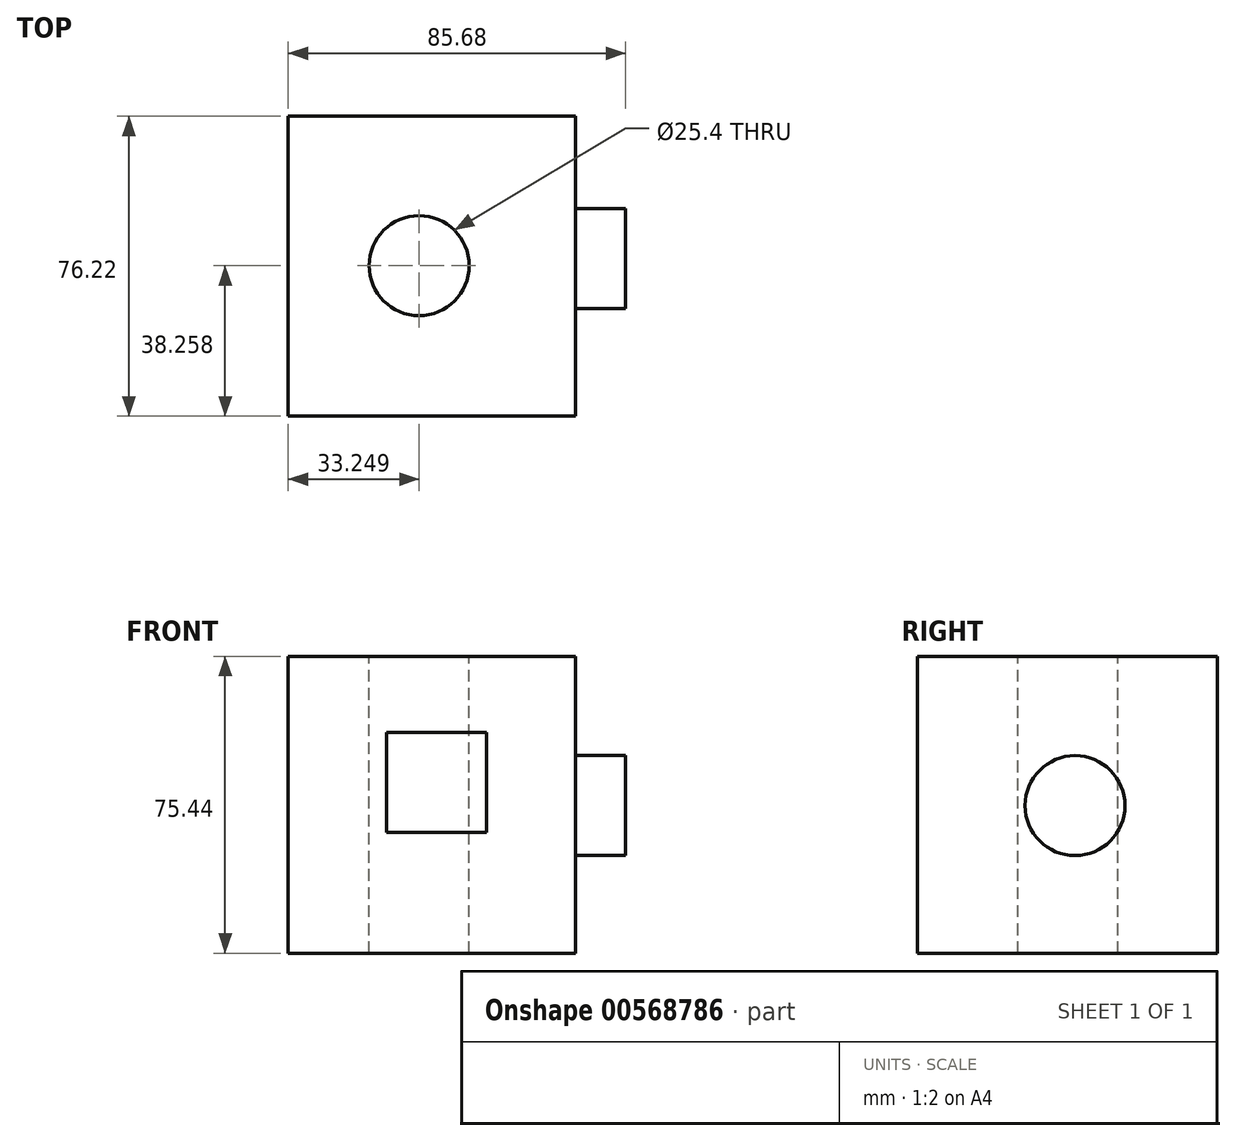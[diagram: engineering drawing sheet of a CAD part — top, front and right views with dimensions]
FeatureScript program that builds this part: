
annotation { "Feature Type Name" : "Feature", "Feature Type Description" : "" }
export const myFeature = defineFeature(function(context is Context, id is Id, definition is map)
    precondition{}
    {
        {
            var Q0;
            Q0=qCreatedBy(makeId("Front.planeOp"),FACE);
            var sketch = newSketch(context, id + "F0", { "sketchPlane" : qUnion([Q0])});
            skLineSegment(sketch, "E0.bottom", {"start": v(3.3, 0) * mm, "end": v(76.28, 0) * mm});
            skLineSegment(sketch, "E0.top", {"start": v(3.3, 75.44) * mm, "end": v(76.28, 75.44) * mm});
            skLineSegment(sketch, "E0.left", {"start": v(3.3, 0) * mm, "end": v(3.3, 75.44) * mm});
            skLineSegment(sketch, "E0.right", {"start": v(76.28, 0) * mm, "end": v(76.28, 75.44) * mm});
            skSolve(sketch);
        }
        {
            var Q0;
            Q0=makeQuery(id+"F0.imprint","IMPRINT",FACE,{"disambiguationData":[TD([[makeQuery(id+"F0.imprint","IMPRINT",EDGE,{"derivedFrom":sQuery(id+"F0.wireOp",EDGE,"E0.bottom")}),1.0]])]});
            extrude(context, id + "F1", {"entities" : qUnion([Q0]), "depth" : 76.2 * mm, "offsetDistance" : 25.4 * mm});
        }
        {
            var Q0;
            Q0=makeQuery(id+"F1.opExtrude","SWEPT_FACE",FACE,{"disambiguationData":[OSD([sQuery(id+"F0.wireOp",EDGE,"E0.top")])]});
            var sketch = newSketch(context, id + "F2", { "sketchPlane" : qUnion([Q0])});
            skPoint(sketch, "E1", {"position": v(36.55, -37.96) * mm});
            skSolve(sketch);
        }
        {
            var Q0;
            Q0=sQuery(id+"F2.wireOp",VERTEX,"E1");
            var Q1;
            Q1=makeQuery(id+"F1.opExtrude","SWEPT_BODY",BODY,{"disambiguationData":[OSD([sQuery(id+"F0.wireOp",EDGE,"E0.bottom"),sQuery(id+"F0.wireOp",EDGE,"E0.top"),sQuery(id+"F0.wireOp",EDGE,"E0.left"),sQuery(id+"F0.wireOp",EDGE,"E0.right")])]});
            hole(context, id + "F3", {"style" : HoleStyle.SIMPLE, "endStyle" : HoleEndStyle.THROUGH, "holeDiameter" : 25.4 * mm, "isTappedThrough" : true, "tappedDepth" : 12.7 * mm, "tapClearance" : 3, "locations" : qUnion([Q0]), "scope" : qUnion([Q1])});
        }
        {
            var Q0;
            Q0=makeQuery(id+"F1.opExtrude","CAP_FACE",FACE,{"disambiguationData":[OSD([sQuery(id+"F0.wireOp",EDGE,"E0.bottom"),sQuery(id+"F0.wireOp",EDGE,"E0.top"),sQuery(id+"F0.wireOp",EDGE,"E0.left"),sQuery(id+"F0.wireOp",EDGE,"E0.right")])],"isStart":false});
            var sketch = newSketch(context, id + "F4", { "sketchPlane" : qUnion([Q0])});
            skLineSegment(sketch, "E2.bottom", {"start": v(28.28, 30.76) * mm, "end": v(53.68, 30.76) * mm});
            skLineSegment(sketch, "E2.top", {"start": v(28.28, 56.16) * mm, "end": v(53.68, 56.16) * mm});
            skLineSegment(sketch, "E2.left", {"start": v(28.28, 30.76) * mm, "end": v(28.28, 56.16) * mm});
            skLineSegment(sketch, "E2.right", {"start": v(53.68, 30.76) * mm, "end": v(53.68, 56.16) * mm});
            skSolve(sketch);
        }
        {
            var Q0;
            Q0 = qSketchRegion(id + "F4", true);
            extrude(context, id + "F5", {"entities" : qUnion([Q0]), "operationType" : NewBodyOperationType.ADD, "depth" : 1 / 50.8 * mm, "offsetDistance" : 25.4 * mm});
        }
        {
            var Q0;
            Q0=makeQuery(id+"F1.opExtrude","SWEPT_FACE",FACE,{"disambiguationData":[OSD([sQuery(id+"F0.wireOp",EDGE,"E0.right")])]});
            var sketch = newSketch(context, id + "F6", { "sketchPlane" : qUnion([Q0])});
            skSolve(sketch);
        }
        {
            var Q0;
            {var subQ0=sQuery(id+"F0.wireOp",EDGE,"E0.right");Q0=makeQuery(id+"F6.imprint","IMPRINT",FACE,{"disambiguationData":[TD([[makeQuery(id+"F6.imprint","IMPRINT",EDGE,{"derivedFrom":makeQuery(id+"F1.opExtrude","CAP_EDGE",EDGE,{"disambiguationData":[OSD([subQ0])],"isStart":true})}),1.0]])]});}
            var sketch = newSketch(context, id + "F7", { "sketchPlane" : qUnion([Q0])});
            skCircle(sketch, "E3", {"center": v(-36.2, 37.5) * mm, "radius": 12.7 * mm});
            skSolve(sketch);
        }
        {
            var Q0;
            Q0=makeQuery(id+"F7.imprint","IMPRINT",FACE,{"disambiguationData":[TD([[makeQuery(id+"F7.imprint","IMPRINT",EDGE,{"derivedFrom":sQuery(id+"F7.wireOp",EDGE,"E3")}),1.0]])]});
            extrude(context, id + "F8", {"entities" : qUnion([Q0]), "operationType" : NewBodyOperationType.ADD, "depth" : 12.7 * mm, "offsetDistance" : 25.4 * mm});
        }
    });
